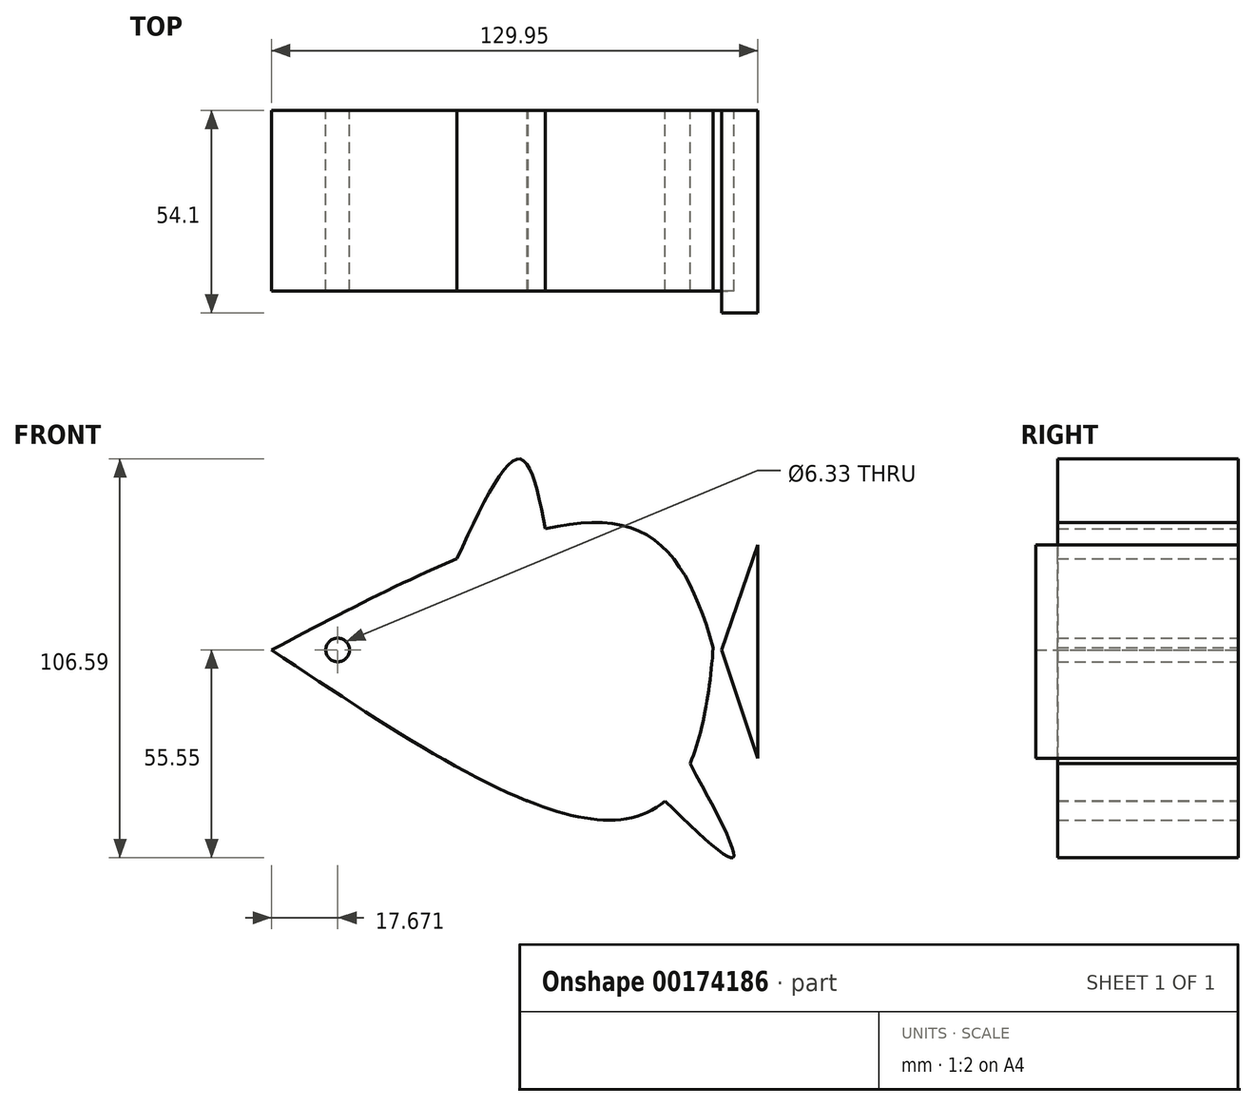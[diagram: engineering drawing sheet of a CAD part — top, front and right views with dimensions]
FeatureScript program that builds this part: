
annotation { "Feature Type Name" : "Feature", "Feature Type Description" : "" }
export const myFeature = defineFeature(function(context is Context, id is Id, definition is map)
    precondition{}
    {
        {
            var Q0;
            Q0=qCreatedBy(makeId("Front.planeOp"),FACE);
            var sketch = newSketch(context, id + "F0", { "sketchPlane" : qUnion([Q0])});
            skFitSpline(sketch, "E0", {"points": [v(-55.67, 0) * mm, v(41.98, 32.03) * mm, v(67.16, -19.22) * mm], "startDerivative": vector(202.37, 106.3) * mm, "endDerivative": vector(35.17, -157.58) * mm});
            skFitSpline(sketch, "E1", {"points": [v(-55.67, 0) * mm, v(52.58, -36.9) * mm, v(62.15, 33.8) * mm, v(62.15, 31.6) * mm, v(62.15, 33.36) * mm], "startDerivative": vector(279.9, -187.1) * mm, "endDerivative": vector(-0.37, 49.56) * mm});
            skFitSpline(sketch, "E2", {"points": [v(-55.67, 0) * mm, v(-35.79, -5.52) * mm, v(-34.9, -4.2) * mm, v(-34.9, -4.64) * mm], "startDerivative": vector(37.37, -15.29) * mm, "endDerivative": vector(-0.35, -6.57) * mm});
            skFitSpline(sketch, "E3", {"points": [v(-6.12, 24.38) * mm, v(10.6, 51.03) * mm, v(17.5, 32.36) * mm], "startDerivative": vector(33.82, 73.34) * mm, "endDerivative": vector(12.45, -62.19) * mm});
            skFitSpline(sketch, "E4", {"points": [v(-10.23, -30.38) * mm, v(0, -51.92) * mm, v(12.66, -40.33) * mm, v(12.9, -40.42) * mm], "startDerivative": vector(13.88, -66.56) * mm, "endDerivative": vector(2.82, -4.4) * mm});
            skFitSpline(sketch, "E5", {"points": [v(-24.74, 6.4) * mm, v(-24.3, -13.03) * mm, v(-29.16, -12.6) * mm], "startDerivative": vector(5.74, -39.34) * mm, "endDerivative": vector(-17.1, 6.41) * mm});
            skFitSpline(sketch, "E6", {"points": [v(49.46, -40.35) * mm, v(67.6, -55.45) * mm, v(56.16, -30.38) * mm], "startDerivative": vector(52.1, -50.58) * mm, "endDerivative": vector(-37.54, 68.98) * mm});
            skSolve(sketch);
        }
        {
            var Q0;
            {var subQ0=sQuery(id+"F0.wireOp",EDGE,"E1");var subQ1=sQuery(id+"F0.wireOp",EDGE,"E0");var subQ2=makeQuery(id+"F0.imprint","INTERSECT",VERTEX,{"disambiguationData":[OD(0.0)],"derivedFrom":[subQ1,subQ0]});Q0=makeQuery(id+"F0.imprint","IMPRINT",FACE,{"disambiguationData":[TD([[makeQuery(id+"F0.imprint","IMPRINT",EDGE,{"disambiguationData":[TD([[subQ2,-1.0]])],"derivedFrom":subQ1}),-1.0]])]});}
            var Q1;
            {var subQ0=sQuery(id+"F0.wireOp",EDGE,"E3");Q1=makeQuery(id+"F0.imprint","IMPRINT",FACE,{"disambiguationData":[TD([[makeQuery(id+"F0.imprint","IMPRINT",EDGE,{"derivedFrom":subQ0}),-1.0]])]});}
            var Q2;
            {var subQ0=sQuery(id+"F0.wireOp",EDGE,"E6");Q2=makeQuery(id+"F0.imprint","IMPRINT",FACE,{"disambiguationData":[TD([[makeQuery(id+"F0.imprint","IMPRINT",EDGE,{"derivedFrom":subQ0}),1.0]])]});}
            extrude(context, id + "F1", {"entities" : qUnion([Q0, Q1, Q2]), "depth" : 48.26 * mm});
        }
        {
            var Q0;
            Q0=qCreatedBy(makeId("Front.planeOp"),FACE);
            var sketch = newSketch(context, id + "F2", { "sketchPlane" : qUnion([Q0])});
            skCircle(sketch, "E7", {"center": v(-38, 0) * mm, "radius": 3.16 * mm});
            skSolve(sketch);
        }
        {
            var Q0;
            Q0=makeQuery(id+"F2.imprint","IMPRINT",FACE,{"disambiguationData":[TD([[makeQuery(id+"F2.imprint","IMPRINT",EDGE,{"derivedFrom":sQuery(id+"F2.wireOp",EDGE,"E7")}),1.0]])]});
            extrude(context, id + "F3", {"entities" : qUnion([Q0]), "operationType" : NewBodyOperationType.REMOVE, "depth" : 219.2 * mm});
        }
        {
            var Q0;
            Q0=qCreatedBy(makeId("Front.planeOp"),FACE);
            var sketch = newSketch(context, id + "F4", { "sketchPlane" : qUnion([Q0])});
            skLineSegment(sketch, "E8", {"start": v(64.56, 0) * mm, "end": v(74.28, 28.06) * mm});
            skLineSegment(sketch, "E9", {"start": v(74.28, 28.06) * mm, "end": v(74.28, -28.94) * mm});
            skLineSegment(sketch, "E10", {"start": v(64.56, 0) * mm, "end": v(74.28, -28.94) * mm});
            skSolve(sketch);
        }
        {
            var Q0;
            Q0=qCreatedBy(makeId("Front.planeOp"),FACE);
            var sketch = newSketch(context, id + "F5", { "sketchPlane" : qUnion([Q0])});
            skFitSpline(sketch, "E11", {"points": [v(46.44, 29.38) * mm, v(59.26, 42.64) * mm, v(57.93, 18.34) * mm], "startDerivative": vector(34.52, 45.69) * mm, "endDerivative": vector(-10.5, -65.22) * mm});
            skSolve(sketch);
        }
        {
            var Q0;
            Q0=sQuery(id+"F5.wireOp",EDGE,"E11");
            extrude(context, id + "F6", {"bodyType" : ToolBodyType.SURFACE, "surfaceEntities" : qUnion([Q0]), "depth" : 47.5 * mm});
        }
        {
            var Q0;
            Q0=makeQuery(id+"F4.imprint","IMPRINT",FACE,{"disambiguationData":[TD([[makeQuery(id+"F4.imprint","IMPRINT",EDGE,{"derivedFrom":sQuery(id+"F4.wireOp",EDGE,"E8")}),-1.0]])]});
            extrude(context, id + "F7", {"entities" : qUnion([Q0]), "depth" : 54.1 * mm});
        }
    });
